# Revit family: BE-5_GENERADO
name_source: partatom
category: Equipos mecánicos
revit_build: Autodesk Revit 2014 (Build: 20130308_1515(x64)
units: mm (PartAtom-declared; Revit-internal decimal feet)

## types (6) — shared parameters
Depth = 382 mm  [stored 1.25328 ft]
Fabricante = SAMMIC S.L.
Foodservice Equipment Identifier = Sí
Height = 537 mm  [stored 1.76181 ft]
Phase = 1
Revision Code = 1
URL = https://www.sammic.com
Width = 310 mm  [stored 1.01706 ft]

## per-type parameters (varying)
| type | Comentarios de tipo | Cycle | Electric Connection Type | FL Amps | Modelo | Specification by Manufacturer | URL Cutsheet | Volts | Weight in Pounds |
| Food mixer BM-5E  230/50-60/1 | Table-top model with 5-lt / qt. bowl. | 50 Hz | EU | 2 A | 1500180 | Designed for light duty use. | http://www.sammic.com | 230 V | 30.2 |
| Food mixer BM-5E 120/60/1 | Table-top model with 5-lt / qt. bowl.

ELECTRICAL DATA:

M Rat:120V/60Hz/1~ (3.5A) | 60 Hz | USA | 3 A | 1500185 | Designed for light duty use. | http://www.sammic.com | 120 V | 30.2 |
| Food mixer BM-5  230/50-60/1 | Table-top model with 5-lt. / qt. bowl. | 50 Hz | EU | 1 A | 1500170 | Designed for medium duty use. | http://www.sammic.com | 230 V | 36.4 |
| Food mixer BM-5/E | Table-top model with 5-lt. / qt. bowl. | 50 Hz |  | 2 A | 1500171 | Designed for medium duty use. | http://www.sammic.com | 230 V | 36.4 |
| Food mixer BM-5 120/50-60/1 | Table-top model with 5-lt. / qt. bowl.

ELECTRICAL DATA:

M Rat:230V/60Hz/3~ (1.6A) | 60 Hz | USA | 2 A | 1500175 | Designed for medium duty use. | http://www.sammic.com | 120 V | 36.4 |
| Food mixer BM-5E 230/50-60/1 KSA | Table-top model with 5-lt. / qt. bowl. | 0 Hz |  | 2 A | 1500179 | Designed for medium duty use. |  | 230 V | 36.4 |

note: column(s) folded — value = type name in every type: Descripción

note: [stored X ft] marks values corroborated as IEEE doubles in the binary element streams (Revit-internal decimal feet)
